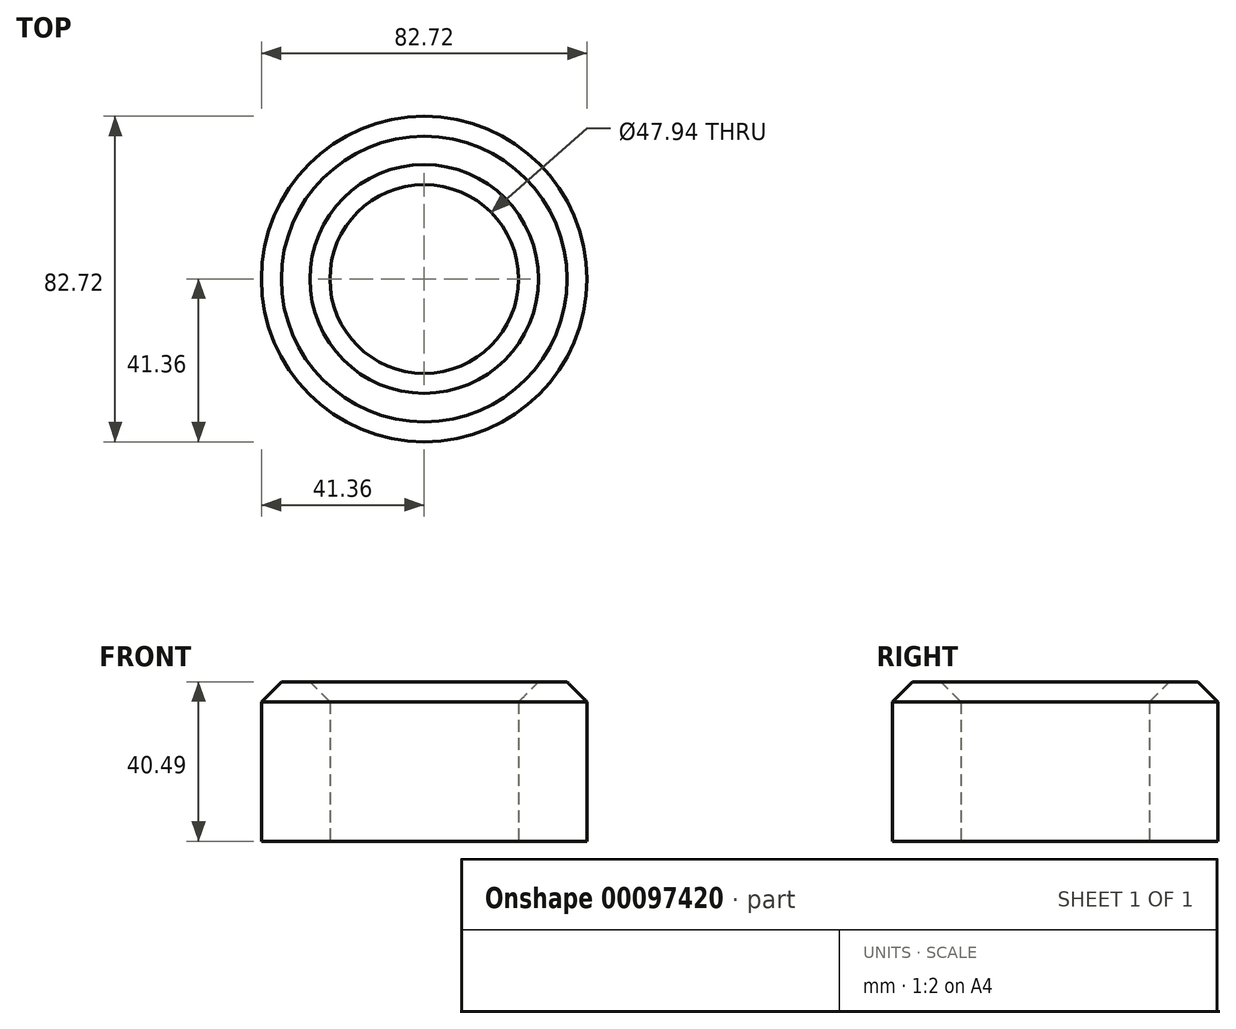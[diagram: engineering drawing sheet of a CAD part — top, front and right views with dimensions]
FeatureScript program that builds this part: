
annotation { "Feature Type Name" : "Feature", "Feature Type Description" : "" }
export const myFeature = defineFeature(function(context is Context, id is Id, definition is map)
    precondition{}
    {
        {
            var Q0;
            Q0=qCreatedBy(makeId("Top.planeOp"),FACE);
            var sketch = newSketch(context, id + "F0", { "sketchPlane" : qUnion([Q0])});
            skCircle(sketch, "E0", {"center": v(0, 0) * mm, "radius": 41.36 * mm});
            skCircle(sketch, "E1", {"center": v(0, 0) * mm, "radius": 23.97 * mm});
            skSolve(sketch);
        }
        {
            var Q0;
            Q0=makeQuery(id+"F0.imprint","IMPRINT",FACE,{"disambiguationData":[TD([[makeQuery(id+"F0.imprint","IMPRINT",EDGE,{"derivedFrom":sQuery(id+"F0.wireOp",EDGE,"E0")}),1.0]])]});
            extrude(context, id + "F1", {"entities" : qUnion([Q0]), "depth" : 40.5 * mm});
        }
        {
            var Q0;
            Q0=makeQuery(id+"F1.opExtrude","CAP_EDGE",EDGE,{"disambiguationData":[OSD([sQuery(id+"F0.wireOp",EDGE,"E0")])],"isStart":false});
            var Q1;
            Q1=makeQuery(id+"F1.opExtrude","CAP_EDGE",EDGE,{"disambiguationData":[OSD([sQuery(id+"F0.wireOp",EDGE,"E1")])],"isStart":false});
            chamfer(context, id + "F2", {"entities" : qUnion([Q0, Q1]), "width" : 5.08 * mm, "tangentPropagation" : true});
        }
    });
